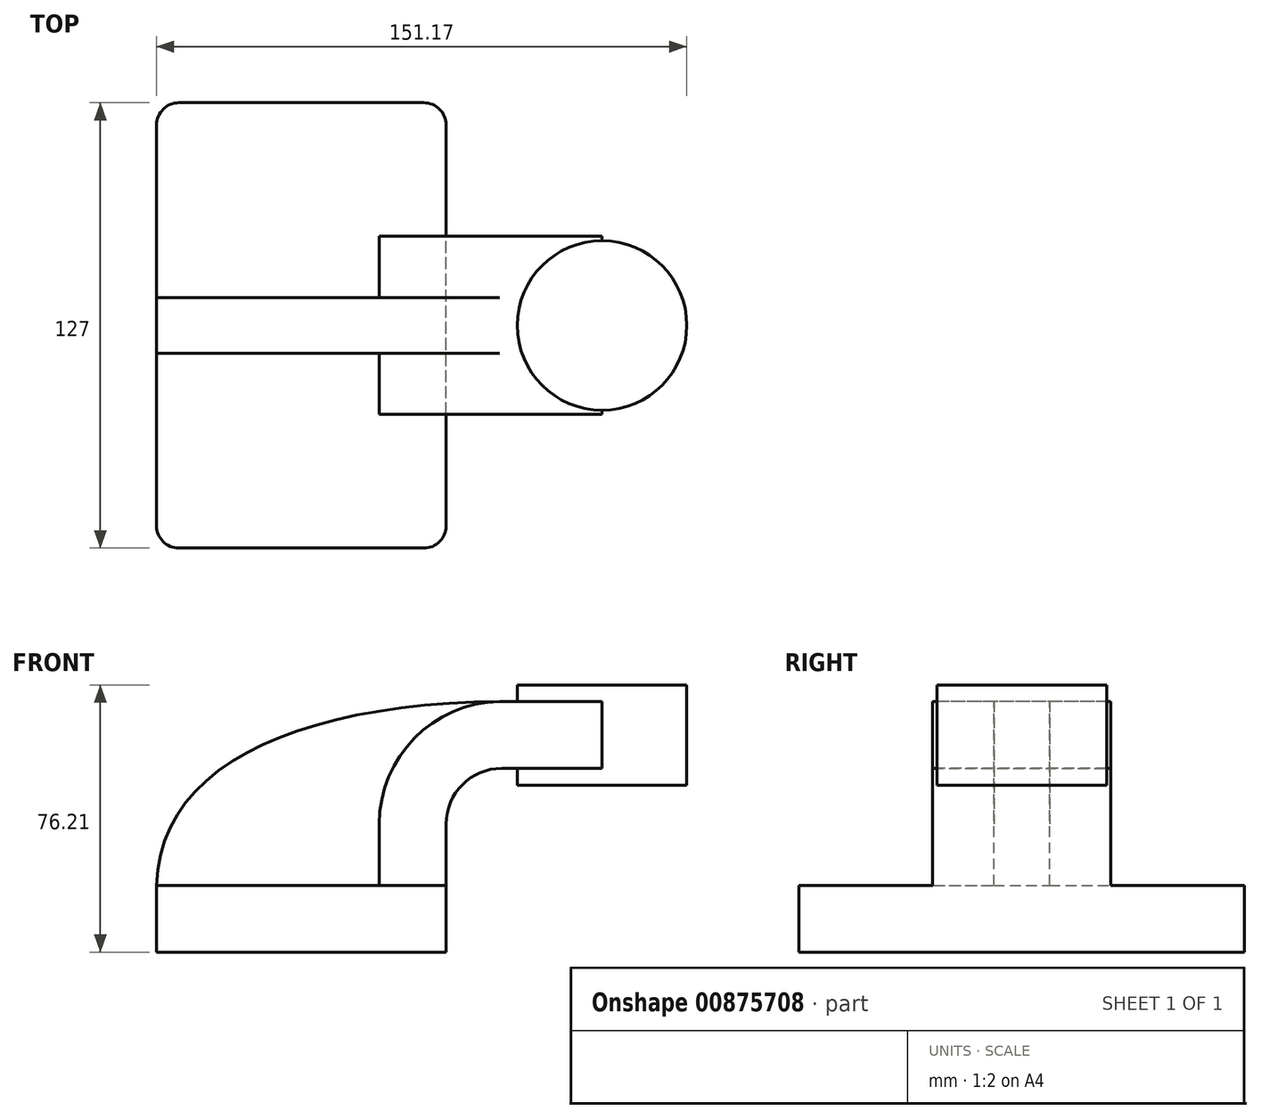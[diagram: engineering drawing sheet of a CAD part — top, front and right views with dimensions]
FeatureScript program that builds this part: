
annotation { "Feature Type Name" : "Feature", "Feature Type Description" : "" }
export const myFeature = defineFeature(function(context is Context, id is Id, definition is map)
    precondition{}
    {
        {
            var Q0;
            Q0=qCreatedBy(makeId("Front.planeOp"),FACE);
            var sketch = newSketch(context, id + "F0", { "sketchPlane" : qUnion([Q0])});
            skLineSegment(sketch, "E0.bottom", {"start": v(-41.28, -9.53) * mm, "end": v(41.28, -9.53) * mm});
            skLineSegment(sketch, "E0.top", {"start": v(-41.28, 9.53) * mm, "end": v(41.28, 9.53) * mm});
            skLineSegment(sketch, "E0.left", {"start": v(-41.28, -9.53) * mm, "end": v(-41.28, 9.53) * mm});
            skLineSegment(sketch, "E0.right", {"start": v(41.28, -9.53) * mm, "end": v(41.28, 9.53) * mm});
            skPoint(sketch, "E0.middle", {"position": v(0, 0) * mm});
            skLineSegment(sketch, "E1.bottom", {"start": v(59.09, 38.1) * mm, "end": v(109.89, 38.1) * mm});
            skLineSegment(sketch, "E1.top", {"start": v(59.09, 66.67) * mm, "end": v(109.89, 66.67) * mm});
            skLineSegment(sketch, "E1.left", {"start": v(59.09, 38.1) * mm, "end": v(59.09, 66.67) * mm});
            skLineSegment(sketch, "E1.right", {"start": v(109.89, 38.1) * mm, "end": v(109.89, 66.67) * mm});
            skPoint(sketch, "E1.middle", {"position": v(84.49, 52.39) * mm});
            skLineSegment(sketch, "E2", {"start": v(41.27, 9.53) * mm, "end": v(41.27, 27) * mm});
            skArc(sketch, "E3", {"start": v(41.27, 27) * mm, "mid": v(45.92, 38.23) * mm, "end": v(57.15, 42.88) * mm});
            skLineSegment(sketch, "E4", {"start": v(57.15, 42.88) * mm, "end": v(85.72, 42.88) * mm});
            skLineSegment(sketch, "E5.0", {"start": v(57.15, 61.93) * mm, "end": v(85.72, 61.93) * mm});
            skArc(sketch, "E5.1", {"start": v(22.23, 27) * mm, "mid": v(32.45, 51.7) * mm, "end": v(57.15, 61.93) * mm});
            skLineSegment(sketch, "E5.2", {"start": v(22.22, 9.53) * mm, "end": v(22.22, 27) * mm});
            skLineSegment(sketch, "E6", {"start": v(85.72, 61.93) * mm, "end": v(85.72, 42.88) * mm});
            skFitSpline(sketch, "E7", {"points": [v(-41.28, 9.53) * mm, v(57.15, 61.93) * mm], "startDerivative": vector(2.6, 104.04) * mm, "endDerivative": vector(171.45, 1.32) * mm});
            skLineSegment(sketch, "E8", {"start": v(85.72, 61.93) * mm, "end": v(85.72, 66.67) * mm});
            skLineSegment(sketch, "E9", {"start": v(85.72, 66.67) * mm, "end": v(85.72, 38.1) * mm});
            skSolve(sketch);
        }
        {
            var Q0;
            Q0=makeQuery(id+"F0.imprint","IMPRINT",FACE,{"disambiguationData":[TD([[makeQuery(id+"F0.imprint","IMPRINT",EDGE,{"derivedFrom":sQuery(id+"F0.wireOp",EDGE,"E0.bottom")}),1.0]])]});
            extrude(context, id + "F1", {"entities" : qUnion([Q0]), "endBound" : BoundingType.SYMMETRIC, "depth" : 127 * mm, "offsetDistance" : 25.4 * mm});
        }
        {
            var Q0;
            {var subQ0=sQuery(id+"F0.wireOp",EDGE,"E2");Q0=makeQuery(id+"F0.imprint","IMPRINT",FACE,{"disambiguationData":[TD([[makeQuery(id+"F0.imprint","IMPRINT",EDGE,{"derivedFrom":subQ0}),1.0]])]});}
            var Q1;
            {var subQ5=sQuery(id+"F0.wireOp",EDGE,"E6");Q1=makeQuery(id+"F0.imprint","IMPRINT",FACE,{"disambiguationData":[TD([[makeQuery(id+"F0.imprint","IMPRINT",EDGE,{"derivedFrom":subQ5}),-1.0]])]});}
            var Q2;
            {var subQ0=sQuery(id+"F0.wireOp",EDGE,"E4");var subQ1=sQuery(id+"F0.wireOp",EDGE,"E1.left");var subQ2=makeQuery(id+"F0.imprint","INTERSECT",VERTEX,{"derivedFrom":[subQ1,subQ0]});Q2=makeQuery(id+"F0.imprint","IMPRINT",FACE,{"disambiguationData":[TD([[makeQuery(id+"F0.imprint","IMPRINT",EDGE,{"disambiguationData":[TD([[subQ2,-1.0]])],"derivedFrom":subQ1}),-1.0]])]});}
            extrude(context, id + "F2", {"entities" : qUnion([Q0, Q1, Q2]), "operationType" : NewBodyOperationType.ADD, "endBound" : BoundingType.SYMMETRIC, "depth" : 50.8 * mm, "offsetDistance" : 25.4 * mm});
        }
        {
            var Q0;
            {var subQ3=sQuery(id+"F0.wireOp",EDGE,"E5.2");Q0=makeQuery(id+"F0.imprint","IMPRINT",FACE,{"disambiguationData":[TD([[makeQuery(id+"F0.imprint","IMPRINT",EDGE,{"derivedFrom":subQ3}),1.0]])]});}
            extrude(context, id + "F3", {"entities" : qUnion([Q0]), "operationType" : NewBodyOperationType.ADD, "endBound" : BoundingType.SYMMETRIC, "depth" : 15.88 * mm, "offsetDistance" : 25.4 * mm});
        }
        {
            var Q0;
            {var subQ4=sQuery(id+"F0.wireOp",EDGE,"E1.right");Q0=makeQuery(id+"F0.imprint","IMPRINT",FACE,{"disambiguationData":[TD([[makeQuery(id+"F0.imprint","IMPRINT",EDGE,{"derivedFrom":subQ4}),1.0]])]});}
            var Q1;
            Q1=sQuery(id+"F0.wireOp",EDGE,"E6");
            revolve(context, id + "F4", {"operationType" : NewBodyOperationType.ADD, "surfaceOperationType" : NewSurfaceOperationType.NEW, "entities" : qUnion([Q0]), "axis" : qUnion([Q1]), "revolveType" : RevolveType.FULL});
        }
        {
            var Q0;
            Q0=makeQuery(id+"F1.opExtrude","CAP_EDGE",EDGE,{"disambiguationData":[OSD([sQuery(id+"F0.wireOp",EDGE,"E0.left")])],"isStart":false});
            var Q1;
            Q1=makeQuery(id+"F1.opExtrude","CAP_EDGE",EDGE,{"disambiguationData":[OSD([sQuery(id+"F0.wireOp",EDGE,"E0.right")])],"isStart":false});
            var Q2;
            Q2=makeQuery(id+"F1.opExtrude","CAP_EDGE",EDGE,{"disambiguationData":[OSD([sQuery(id+"F0.wireOp",EDGE,"E0.right")])],"isStart":true});
            var Q3;
            Q3=makeQuery(id+"F1.opExtrude","CAP_EDGE",EDGE,{"disambiguationData":[OSD([sQuery(id+"F0.wireOp",EDGE,"E0.left")])],"isStart":true});
            fillet(context, id + "F5", {"entities" : qUnion([Q0, Q1, Q2, Q3]), "radius" : 6.35 * mm, "tangentPropagation" : true, "allowEdgeOverflow" : false});
        }
    });
